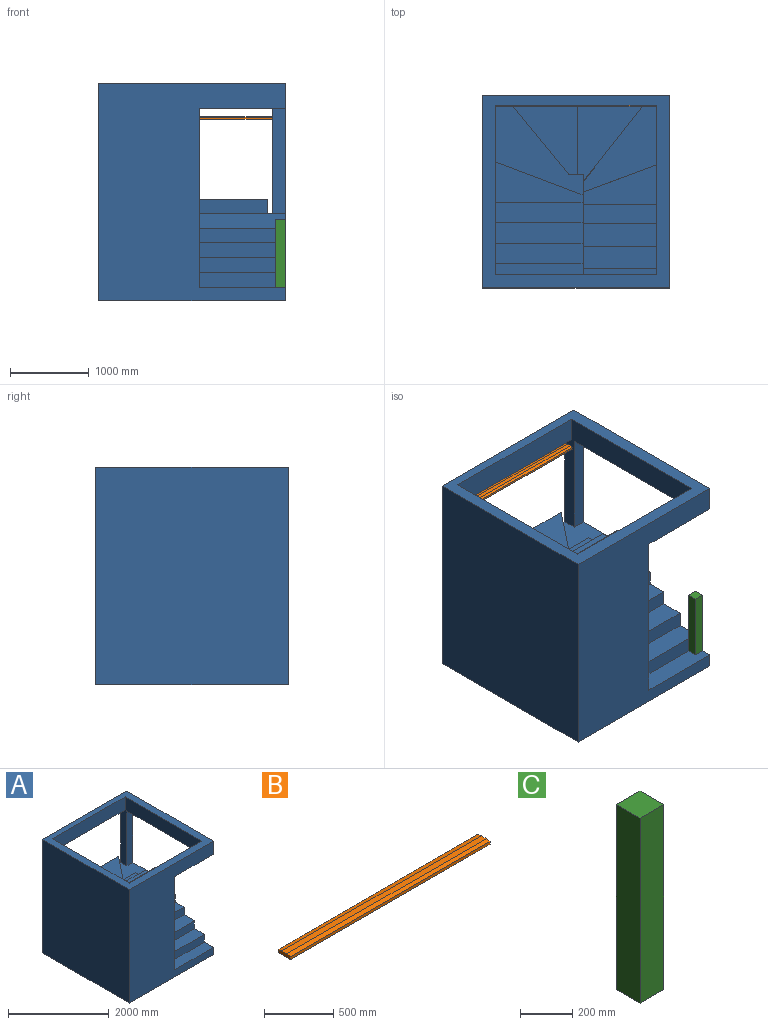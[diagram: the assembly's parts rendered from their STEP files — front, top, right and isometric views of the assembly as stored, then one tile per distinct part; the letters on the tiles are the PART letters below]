
ASSEMBLY  parts=3 mates=2
PART A: 42 faces, bbox 2362.2x2438.4x2755.9 mm
  f0: plane 2273.3x1117.6mm, normal (1,0,0), area 1856044.7mm2, adj f2,f4,f10,f11,f12,f13,f14,f15
  f1: plane 2393.95x1435.1mm, normal (1,0,0), area 2176527.9mm2, adj f2,f6,f9,f10,f11,f12,f13,f14
  f2: plane 1111.25x139.7mm, normal (0,0,1), area 155241.6mm2, adj f0,f1,f19,f37
  f3: plane 1333.5x165.1mm, normal (0,-1,0), area 220160.8mm2, adj f20,f31,f32,f38
  f4: plane 2755.9x2362.2mm, normal (0,1,0), area 4346201mm2, adj f0,f5,f7,f8,f10,f20,f31,f32
  f5: plane 2755.9x2438.4mm, normal (-1,0,0), area 6719986.6mm2, adj f4,f6,f7,f41
  f6: plane 2755.9x2362.2mm, normal (0,-1,0), area 4034024.2mm2, adj f1,f5,f7,f20,f21,f38,f41
  f7: plane 2438.4x2362.2mm, normal (0,0,-1), area 5759988.5mm2, adj f4,f5,f6,f20
  f8: plane 1003.3x825.5mm, normal (0.77,0.64,0), area 231007.4mm2, adj f4,f9,f10,f36
  f9: plane 355.6x177.8mm, normal (0,1,0), area 45161.2mm2, adj f1,f8,f10,f34,f35,f36
  f10: plane 1257.3x1111.25mm, normal (0,0,1), area 571813.4mm2, adj f0,f1,f4,f8,f9,f11
  f11: plane 1111.25x419.1mm, normal (0.35,0.94,0), area 211164.8mm2, adj f0,f1,f10,f12
  f12: plane 1111.25x514.35mm, normal (0,0,1), area 338709mm2, adj f0,f1,f11,f13
  f13: plane 1111.25x177.8mm, normal (0,1,0), area 197580.2mm2, adj f0,f1,f12,f14
  f14: plane 1111.25x260.35mm, normal (0,0,1), area 289313.9mm2, adj f0,f1,f13,f15
  f15: plane 1111.25x190.5mm, normal (0,1,0), area 211693.1mm2, adj f0,f1,f14,f16
  f16: plane 1111.25x266.7mm, normal (0,0,1), area 296370.4mm2, adj f0,f1,f15,f17
  f17: plane 1111.25x190.5mm, normal (0,1,0), area 211693.1mm2, adj f0,f1,f16,f18
  f18: plane 1111.25x254mm, normal (0,0,1), area 282257.5mm2, adj f0,f1,f17,f19
  f19: plane 1111.25x190.5mm, normal (0,1,0), area 211693.1mm2, adj f0,f1,f2,f18
  f20: plane 2755.9x2438.4mm, normal (1,0,0), area 2899187.8mm2, adj f3,f4,f6,f7,f21,f22,f23,f24
  f21: plane 1092.2x254mm, normal (0,0,1), area 277418.8mm2, adj f1,f6,f20,f22
  f22: plane 1092.2x190.5mm, normal (0,-1,0), area 208064.1mm2, adj f1,f20,f21,f23
  f23: plane 1092.2x279.4mm, normal (0,0,1), area 305160.7mm2, adj f1,f20,f22,f24
  f24: plane 1092.2x190.5mm, normal (0,-1,0), area 208064.1mm2, adj f1,f20,f23,f25
  f25: plane 1092.2x292.1mm, normal (0,0,1), area 319031.6mm2, adj f1,f20,f24,f26
  f26: plane 1092.2x184.15mm, normal (0,-1,0), area 201128.6mm2, adj f1,f20,f25,f27
  f27: plane 1092.2x241.3mm, normal (0,0,1), area 263547.9mm2, adj f1,f20,f26,f28
  f28: plane 1092.2x184.15mm, normal (0,-1,0), area 201128.6mm2, adj f1,f20,f27,f29
  f29: plane 1092.2x558.8mm, normal (0,0,1), area 388386.3mm2, adj f1,f20,f28,f30
  f30: plane 1092.2x406.4mm, normal (0.35,-0.94,0), area 214600.9mm2, adj f1,f20,f29,f31
  f31: plane 1219.2x1092.2mm, normal (0,0,1), area 609756.8mm2, adj f1,f3,f4,f20,f30,f32,f33
  f32: plane 2273.3x1651mm, normal (-1,0,0), area 912094.9mm2, adj f3,f4,f31,f37,f38,f39,f40,f41
  f33: plane 1092.2x863.6mm, normal (0.78,-0.62,0), area 247564.1mm2, adj f1,f4,f31,f34
  f34: plane 1092.2x939.8mm, normal (0,0,1), area 548063.4mm2, adj f1,f4,f9,f33,f35
  f35: plane 1003.3x177.8mm, normal (1,0,0), area 178386.7mm2, adj f4,f9,f34,f36
  f36: plane 1003.3x927.1mm, normal (0,0,1), area 516047.4mm2, adj f4,f8,f9,f35
  f37: plane 2038.35x317.5mm, normal (0,1,0), area 506047.4mm2, adj f0,f1,f2,f32,f38,f41
  f38: plane 2266.95x1092.2mm, normal (0,0,-1), area 527337.7mm2, adj f1,f3,f6,f20,f32,f37
  f39: plane 2038.35x120.65mm, normal (0,0,-1), area 245926.9mm2, adj f0,f4,f32,f40
  f40: plane 2038.35x317.5mm, normal (0,-1,0), area 647176.1mm2, adj f0,f32,f39,f41
  f41: plane 2438.4x2362.2mm, normal (0,0,1), area 1372134.4mm2, adj f0,f4,f5,f6,f20,f32,f37,f40
PART B: 8 faces, bbox 2038.4x127x31.8 mm
  f0: plane 2038.35x127mm, normal (0,0,-1), area 258870.4mm2, adj f1,f5,f6,f7
  f1: plane 2038.35x25.03mm, normal (0,1,0), area 51023.9mm2, adj f0,f2,f6,f7
  f2: plane 2038.35x38.1mm, normal (0,0.17,0.98), area 78859.2mm2, adj f1,f3,f6,f7
  f3: plane 2038.35x50.8mm, normal (0,0,1), area 103548.2mm2, adj f2,f4,f6,f7
  f4: plane 2038.35x38.1mm, normal (0,-0.17,0.98), area 78859.2mm2, adj f3,f5,f6,f7
  f5: plane 2038.35x25.03mm, normal (0,-1,0), area 51023.9mm2, adj f0,f4,f6,f7
  f6: plane 127x31.75mm, normal (1,0,0), area 3776.3mm2, adj f0,f1,f2,f3,f4,f5
  f7: plane 127x31.75mm, normal (-1,0,0), area 3776.3mm2, adj f0,f1,f2,f3,f4,f5
PART C: 6 faces, bbox 127x127x863.6 mm
  f0: plane 863.6x127mm, normal (0,-1,0), area 109677.2mm2, adj f1,f3,f4,f5
  f1: plane 863.6x127mm, normal (1,0,0), area 109677.2mm2, adj f0,f2,f4,f5
  f2: plane 863.6x127mm, normal (0,1,0), area 109677.2mm2, adj f1,f3,f4,f5
  f3: plane 863.6x127mm, normal (-1,0,0), area 109677.2mm2, adj f0,f2,f4,f5
  f4: plane 127x127mm, normal (0,0,1), area 16129mm2, adj f0,f1,f2,f3
  f5: plane 127x127mm, normal (0,0,-1), area 16129mm2, adj f0,f1,f2,f3
PLACE A at identity fixed
PLACE B t=(-2203.45,-72.83,2300.65)mm
PLACE C rot(axis=(0,0,-1),90deg) t=(-63.5,-2247.9,171.45)mm
MATE planar B.f6 <-> A.f32  axis (1,0,0) through (-165.1,-72.83,2315.6)mm
MATE fastened A.f21 <-> C.f5  axis (0,0,1) through (0,-2184.4,171.45)mm
